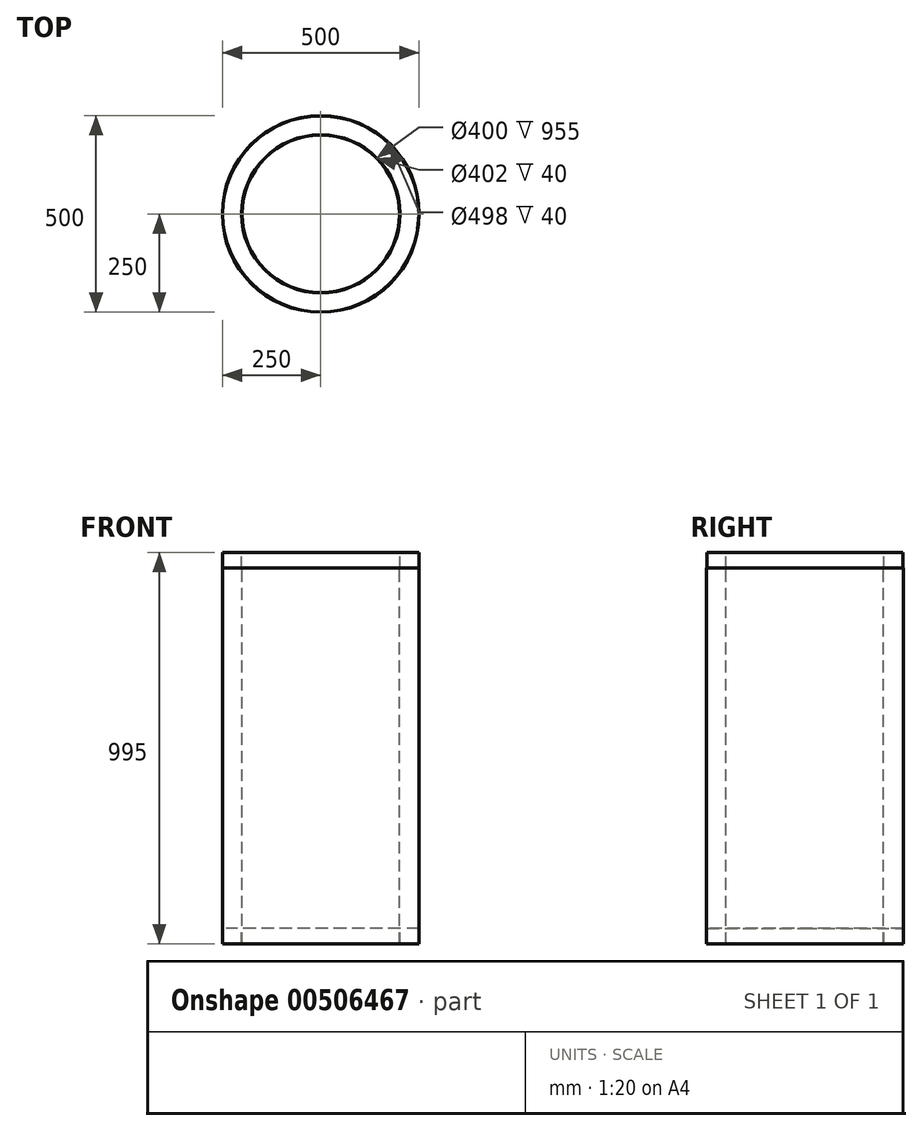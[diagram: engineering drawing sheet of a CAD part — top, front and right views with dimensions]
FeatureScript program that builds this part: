
annotation { "Feature Type Name" : "Feature", "Feature Type Description" : "" }
export const myFeature = defineFeature(function(context is Context, id is Id, definition is map)
    precondition{}
    {
        {
            var Q0;
            Q0=qCreatedBy(makeId("Front.planeOp"),FACE);
            var sketch = newSketch(context, id + "F0", { "sketchPlane" : qUnion([Q0])});
            skLineSegment(sketch, "E0", {"start": v(0, 452.89) * mm, "end": v(0, -450.9) * mm, "construction": true});
            skLineSegment(sketch, "E1", {"start": v(-200, -411.7) * mm, "end": v(-200, 543.3) * mm});
            skLineSegment(sketch, "E2", {"start": v(-200, 543.3) * mm, "end": v(-201, 543.3) * mm});
            skLineSegment(sketch, "E3", {"start": v(-201, 543.3) * mm, "end": v(-201, 583.3) * mm});
            skLineSegment(sketch, "E4", {"start": v(-201, 583.3) * mm, "end": v(-249, 583.3) * mm});
            skLineSegment(sketch, "E5", {"start": v(-249, 583.3) * mm, "end": v(-249, 543.3) * mm});
            skLineSegment(sketch, "E6", {"start": v(-249, 543.3) * mm, "end": v(-250, 543.3) * mm});
            skLineSegment(sketch, "E7", {"start": v(-250, 543.3) * mm, "end": v(-250, -411.7) * mm});
            skLineSegment(sketch, "E8", {"start": v(-250, -411.7) * mm, "end": v(-249, -411.7) * mm});
            skLineSegment(sketch, "E9", {"start": v(-249, -411.7) * mm, "end": v(-249, -371.7) * mm});
            skLineSegment(sketch, "E10", {"start": v(-249, -371.7) * mm, "end": v(-201, -371.7) * mm});
            skLineSegment(sketch, "E11", {"start": v(-201, -371.7) * mm, "end": v(-201, -411.7) * mm});
            skLineSegment(sketch, "E12", {"start": v(-201, -411.7) * mm, "end": v(-200, -411.7) * mm});
            skSolve(sketch);
        }
        {
            var Q0;
            Q0=qSketchRegion(id+"F0",true);
            var Q1;
            Q1=sQuery(id+"F0.wireOp",EDGE,"E0");
            revolve(context, id + "F1", {"entities" : qUnion([Q0]), "axis" : qUnion([Q1]), "revolveType" : RevolveType.FULL});
        }
    });
